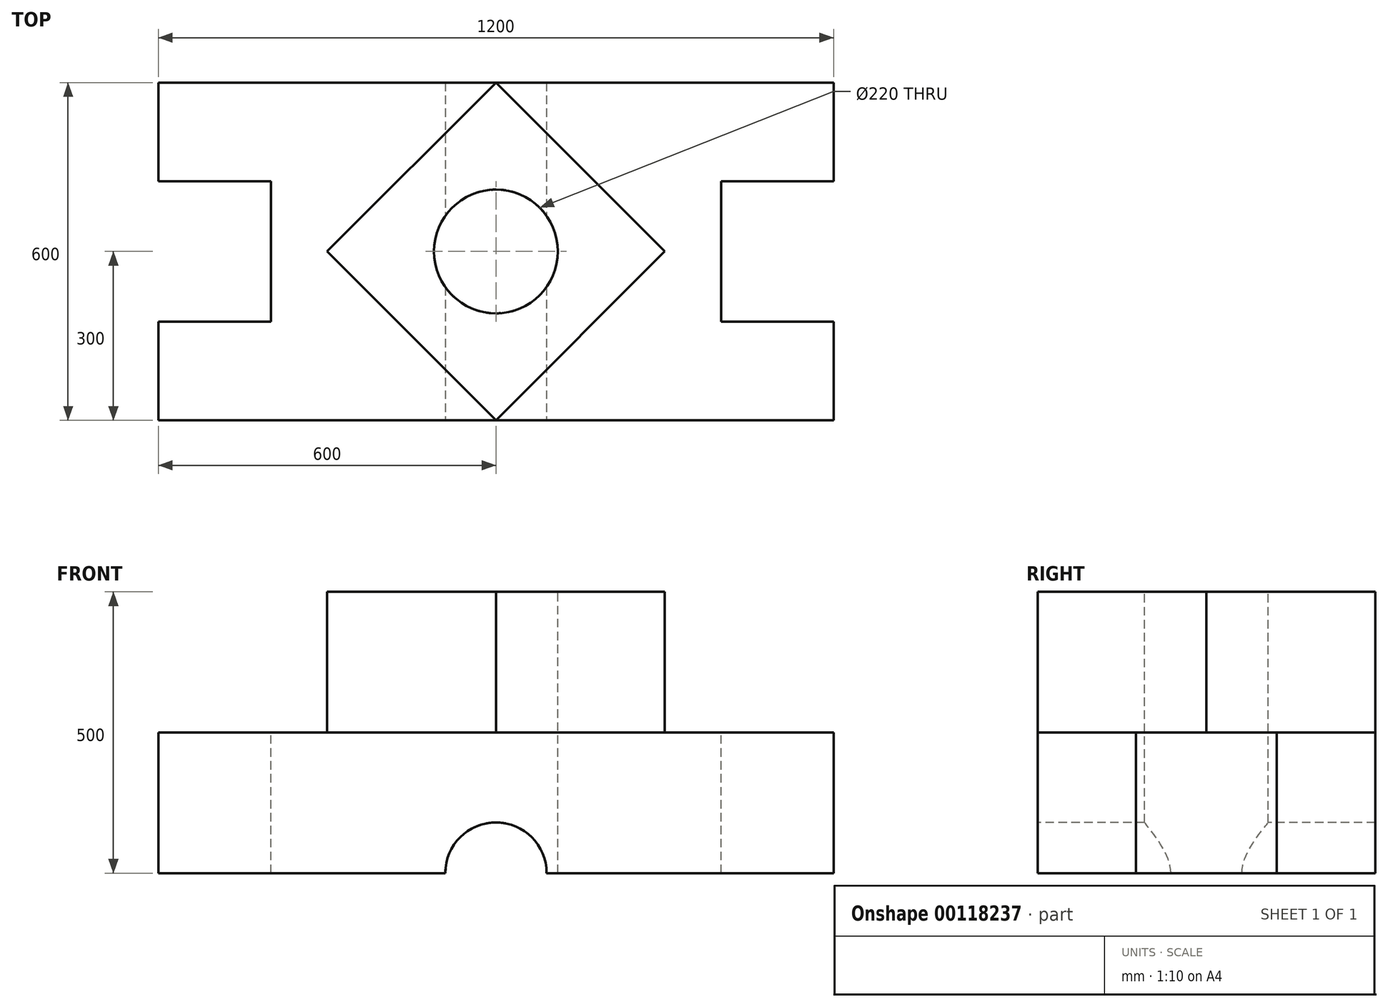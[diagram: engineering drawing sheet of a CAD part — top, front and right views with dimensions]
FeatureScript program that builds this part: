
annotation { "Feature Type Name" : "Feature", "Feature Type Description" : "" }
export const myFeature = defineFeature(function(context is Context, id is Id, definition is map)
    precondition{}
    {
        {
            var Q0;
            Q0=qCreatedBy(makeId("Top.planeOp"),FACE);
            var sketch = newSketch(context, id + "F0", { "sketchPlane" : qUnion([Q0])});
            skLineSegment(sketch, "E0.bottom", {"start": v(600, 300) * mm, "end": v(-600, 300) * mm});
            skLineSegment(sketch, "E0.top", {"start": v(600, -300) * mm, "end": v(-600, -300) * mm});
            skLineSegment(sketch, "E0.left", {"start": v(600, 300) * mm, "end": v(600, -300) * mm});
            skLineSegment(sketch, "E0.right", {"start": v(-600, 300) * mm, "end": v(-600, -300) * mm});
            skPoint(sketch, "E0.middle", {"position": v(0, 0) * mm});
            skSolve(sketch);
        }
        {
            var Q0;
            Q0=makeQuery(id+"F0.imprint","IMPRINT",FACE,{"disambiguationData":[TD([[makeQuery(id+"F0.imprint","IMPRINT",EDGE,{"derivedFrom":sQuery(id+"F0.wireOp",EDGE,"E0.bottom")}),1.0]])]});
            extrude(context, id + "F1", {"entities" : qUnion([Q0]), "depth" : 250 * mm});
        }
        {
            var Q0;
            Q0=makeQuery(id+"F1.opExtrude","CAP_FACE",FACE,{"disambiguationData":[OSD([sQuery(id+"F0.wireOp",EDGE,"E0.bottom"),sQuery(id+"F0.wireOp",EDGE,"E0.top"),sQuery(id+"F0.wireOp",EDGE,"E0.left"),sQuery(id+"F0.wireOp",EDGE,"E0.right")])],"isStart":false});
            var sketch = newSketch(context, id + "F2", { "sketchPlane" : qUnion([Q0])});
            skLineSegment(sketch, "E1.bottom", {"start": v(-400, 125) * mm, "end": v(-800, 125) * mm});
            skLineSegment(sketch, "E1.top", {"start": v(-400, -125) * mm, "end": v(-800, -125) * mm});
            skLineSegment(sketch, "E1.left", {"start": v(-400, 125) * mm, "end": v(-400, -125) * mm});
            skLineSegment(sketch, "E1.right", {"start": v(-800, 125) * mm, "end": v(-800, -125) * mm});
            skPoint(sketch, "E1.middle", {"position": v(-600, 0) * mm});
            skLineSegment(sketch, "E2", {"start": v(0, 300) * mm, "end": v(0, -300) * mm, "construction": true});
            skLineSegment(sketch, "E3.MirrorCS", {"start": v(400, 125) * mm, "end": v(800, 125) * mm});
            skLineSegment(sketch, "E4.MirrorCS", {"start": v(400, 125) * mm, "end": v(400, -125) * mm});
            skLineSegment(sketch, "E5.MirrorCS", {"start": v(400, -125) * mm, "end": v(800, -125) * mm});
            skLineSegment(sketch, "E6.MirrorCS", {"start": v(800, 125) * mm, "end": v(800, -125) * mm});
            skSolve(sketch);
        }
        {
            var Q0;
            {var subQ0=sQuery(id+"F2.wireOp",EDGE,"E1.left");Q0=makeQuery(id+"F2.imprint","IMPRINT",FACE,{"disambiguationData":[TD([[makeQuery(id+"F2.imprint","IMPRINT",EDGE,{"derivedFrom":subQ0}),-1.0]])]});}
            var Q1;
            {var subQ0=sQuery(id+"F2.wireOp",EDGE,"E4.MirrorCS");Q1=makeQuery(id+"F2.imprint","IMPRINT",FACE,{"disambiguationData":[TD([[makeQuery(id+"F2.imprint","IMPRINT",EDGE,{"derivedFrom":subQ0}),1.0]])]});}
            extrude(context, id + "F3", {"entities" : qUnion([Q0, Q1]), "operationType" : NewBodyOperationType.REMOVE, "endBound" : BoundingType.THROUGH_ALL, "oppositeDirection" : true, "depth" : 25 * mm});
        }
        {
            var Q0;
            Q0=makeQuery(id+"F1.opExtrude","CAP_FACE",FACE,{"disambiguationData":[OSD([sQuery(id+"F0.wireOp",EDGE,"E0.bottom"),sQuery(id+"F0.wireOp",EDGE,"E0.top"),sQuery(id+"F0.wireOp",EDGE,"E0.left"),sQuery(id+"F0.wireOp",EDGE,"E0.right")])],"isStart":false});
            var sketch = newSketch(context, id + "F4", { "sketchPlane" : qUnion([Q0])});
            skLineSegment(sketch, "E7", {"start": v(0, -300) * mm, "end": v(300, 0) * mm});
            skLineSegment(sketch, "E8", {"start": v(300, 0) * mm, "end": v(0, 300) * mm});
            skLineSegment(sketch, "E9", {"start": v(0, 300) * mm, "end": v(-300, 0) * mm});
            skLineSegment(sketch, "E10", {"start": v(-300, 0) * mm, "end": v(0, -300) * mm});
            skSolve(sketch);
        }
        {
            var Q0;
            Q0 = qSketchRegion(id + "F4", true);
            extrude(context, id + "F5", {"entities" : qUnion([Q0]), "operationType" : NewBodyOperationType.ADD, "depth" : 250 * mm});
        }
        {
            var Q0;
            Q0=makeQuery(id+"F5.opExtrude","CAP_FACE",FACE,{"disambiguationData":[OSD([sQuery(id+"F4.wireOp",EDGE,"E7"),sQuery(id+"F4.wireOp",EDGE,"E8"),sQuery(id+"F4.wireOp",EDGE,"E9"),sQuery(id+"F4.wireOp",EDGE,"E10")])],"isStart":false});
            var sketch = newSketch(context, id + "F6", { "sketchPlane" : qUnion([Q0])});
            skCircle(sketch, "E11", {"center": v(0, 0) * mm, "radius": 110 * mm});
            skSolve(sketch);
        }
        {
            var Q0;
            Q0=makeQuery(id+"F6.imprint","IMPRINT",FACE,{"disambiguationData":[TD([[makeQuery(id+"F6.imprint","IMPRINT",EDGE,{"derivedFrom":sQuery(id+"F6.wireOp",EDGE,"E11")}),1.0]])]});
            extrude(context, id + "F7", {"entities" : qUnion([Q0]), "operationType" : NewBodyOperationType.REMOVE, "endBound" : BoundingType.THROUGH_ALL, "oppositeDirection" : true, "depth" : 25 * mm});
        }
        {
            var Q0;
            Q0=makeQuery(id+"F1.opExtrude","SWEPT_FACE",FACE,{"disambiguationData":[OSD([sQuery(id+"F0.wireOp",EDGE,"E0.top")])]});
            var sketch = newSketch(context, id + "F8", { "sketchPlane" : qUnion([Q0])});
            skCircle(sketch, "E12", {"center": v(0, 0) * mm, "radius": 90 * mm});
            skSolve(sketch);
        }
        {
            var Q0;
            {var subQ0=sQuery(id+"F8.wireOp",EDGE,"E12");var subQ1=makeQuery(id+"F1.opExtrude","CAP_EDGE",EDGE,{"disambiguationData":[OSD([sQuery(id+"F0.wireOp",EDGE,"E0.top")])],"isStart":true});var subQ2=makeQuery(id+"F8.imprint","INTERSECT",VERTEX,{"disambiguationData":[OD(0.0)],"derivedFrom":[subQ1,subQ0]});Q0=makeQuery(id+"F8.imprint","IMPRINT",FACE,{"disambiguationData":[TD([[makeQuery(id+"F8.imprint","IMPRINT",EDGE,{"disambiguationData":[TD([[subQ2,-1.0]])],"derivedFrom":subQ0}),1.0]])]});}
            extrude(context, id + "F9", {"entities" : qUnion([Q0]), "operationType" : NewBodyOperationType.REMOVE, "endBound" : BoundingType.THROUGH_ALL, "oppositeDirection" : true, "depth" : 25 * mm});
        }
    });
